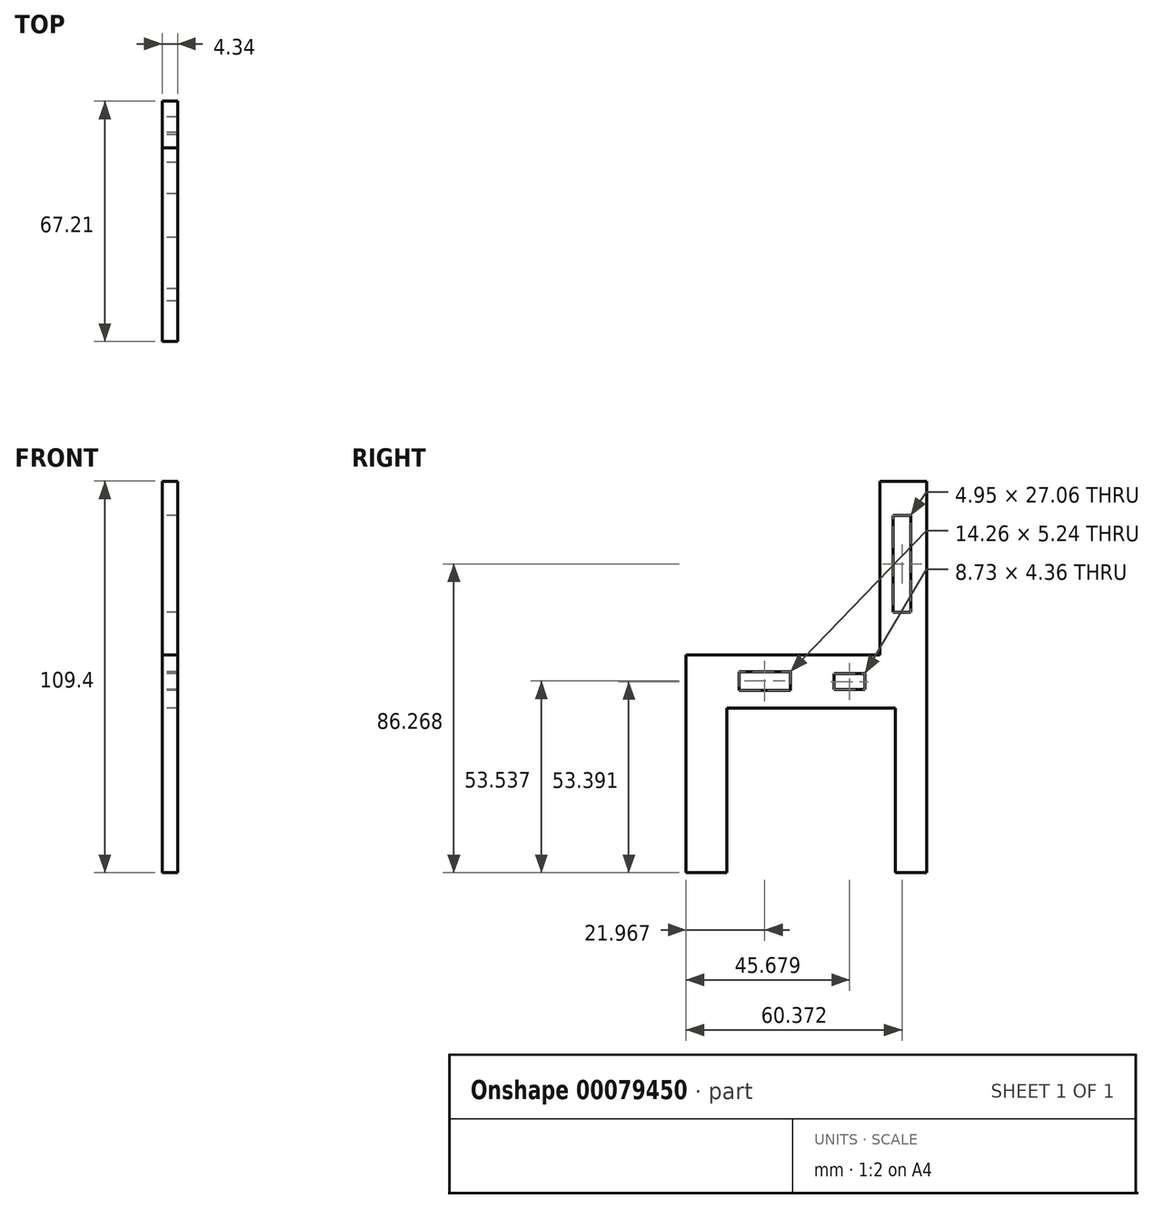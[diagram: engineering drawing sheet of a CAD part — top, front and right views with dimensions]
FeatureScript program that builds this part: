
annotation { "Feature Type Name" : "Feature", "Feature Type Description" : "" }
export const myFeature = defineFeature(function(context is Context, id is Id, definition is map)
    precondition{}
    {
        {
            var Q0;
            Q0=qCreatedBy(makeId("Right.planeOp"),FACE);
            var sketch = newSketch(context, id + "F0", { "sketchPlane" : qUnion([Q0])});
            skLineSegment(sketch, "E0", {"start": v(22.84, 48.58) * mm, "end": v(22.84, -60.82) * mm});
            skLineSegment(sketch, "E1", {"start": v(22.84, -60.82) * mm, "end": v(14.11, -60.82) * mm});
            skLineSegment(sketch, "E2", {"start": v(14.11, -60.82) * mm, "end": v(14.11, -14.85) * mm});
            skLineSegment(sketch, "E3", {"start": v(14.11, -14.85) * mm, "end": v(-33.02, -14.85) * mm});
            skLineSegment(sketch, "E4", {"start": v(-33.02, -14.85) * mm, "end": v(-33.02, -60.82) * mm});
            skPoint(sketch, "E4.endSnap0", {"position": v(18.48, -60.82) * mm});
            skLineSegment(sketch, "E5", {"start": v(-33.02, -60.82) * mm, "end": v(-44.37, -60.82) * mm});
            skLineSegment(sketch, "E6", {"start": v(-44.37, -60.82) * mm, "end": v(-44.37, 0) * mm});
            skLineSegment(sketch, "E7", {"start": v(-44.37, 0) * mm, "end": v(9.75, 0) * mm});
            skLineSegment(sketch, "E8", {"start": v(9.75, 0) * mm, "end": v(9.75, 48.58) * mm});
            skLineSegment(sketch, "E9", {"start": v(9.75, 48.58) * mm, "end": v(22.84, 48.58) * mm});
            skLineSegment(sketch, "E10.bottom", {"start": v(13.53, 38.98) * mm, "end": v(18.48, 38.98) * mm});
            skLineSegment(sketch, "E10.top", {"start": v(13.53, 11.92) * mm, "end": v(18.48, 11.92) * mm});
            skLineSegment(sketch, "E10.left", {"start": v(13.53, 38.98) * mm, "end": v(13.53, 11.92) * mm});
            skLineSegment(sketch, "E10.right", {"start": v(18.48, 38.98) * mm, "end": v(18.48, 11.92) * mm});
            skLineSegment(sketch, "E11.bottom", {"start": v(-29.53, -4.66) * mm, "end": v(-15.27, -4.66) * mm});
            skLineSegment(sketch, "E11.top", {"start": v(-29.53, -9.9) * mm, "end": v(-15.27, -9.9) * mm});
            skLineSegment(sketch, "E11.left", {"start": v(-29.53, -4.66) * mm, "end": v(-29.53, -9.9) * mm});
            skLineSegment(sketch, "E11.right", {"start": v(-15.27, -4.66) * mm, "end": v(-15.27, -9.9) * mm});
            skLineSegment(sketch, "E12.bottom", {"start": v(-3.05, -5.25) * mm, "end": v(5.67, -5.25) * mm});
            skLineSegment(sketch, "E12.top", {"start": v(-3.05, -9.61) * mm, "end": v(5.67, -9.61) * mm});
            skLineSegment(sketch, "E12.left", {"start": v(-3.05, -5.25) * mm, "end": v(-3.05, -9.61) * mm});
            skLineSegment(sketch, "E12.right", {"start": v(5.67, -5.25) * mm, "end": v(5.67, -9.61) * mm});
            skSolve(sketch);
        }
        {
            var Q0;
            Q0 = qSketchRegion(id + "F0", true);
            extrude(context, id + "F1", {"entities" : qUnion([Q0]), "depth" : 4.34 * mm});
        }
    });
